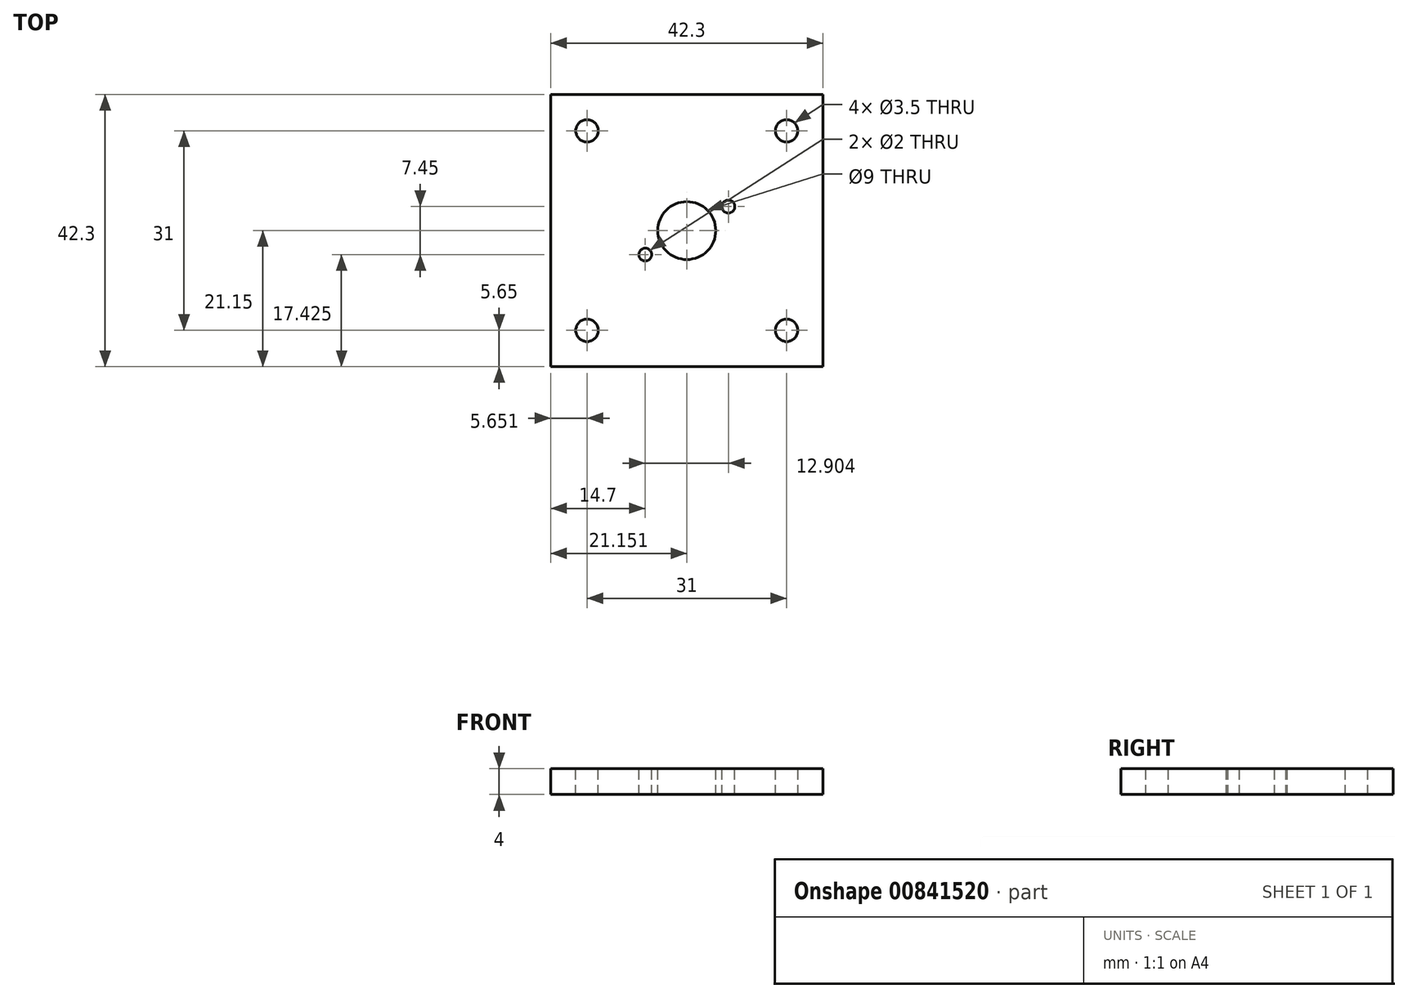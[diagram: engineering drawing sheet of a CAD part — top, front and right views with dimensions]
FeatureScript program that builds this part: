
annotation { "Feature Type Name" : "Feature", "Feature Type Description" : "" }
export const myFeature = defineFeature(function(context is Context, id is Id, definition is map)
    precondition{}
    {
        {
            var Q0;
            Q0=qCreatedBy(makeId("Top.planeOp"),FACE);
            var sketch = newSketch(context, id + "F0", { "sketchPlane" : qUnion([Q0])});
            skLineSegment(sketch, "E0.bottom", {"start": v(-22.2, 20.42) * mm, "end": v(20.1, 20.42) * mm});
            skLineSegment(sketch, "E0.top", {"start": v(-22.2, -21.88) * mm, "end": v(20.1, -21.88) * mm});
            skLineSegment(sketch, "E0.left", {"start": v(-22.2, 20.42) * mm, "end": v(-22.2, -21.88) * mm});
            skLineSegment(sketch, "E0.right", {"start": v(20.1, 20.42) * mm, "end": v(20.1, -21.88) * mm});
            skSolve(sketch);
        }
        {
            var Q0;
            Q0=makeQuery(id+"F0.imprint","IMPRINT",FACE,{"disambiguationData":[TD([[makeQuery(id+"F0.imprint","IMPRINT",EDGE,{"derivedFrom":sQuery(id+"F0.wireOp",EDGE,"E0.bottom")}),-1.0]])]});
            extrude(context, id + "F1", {"entities" : qUnion([Q0]), "depth" : 4 * mm, "offsetDistance" : 25 * mm});
        }
        {
            var Q0;
            Q0=makeQuery(id+"F1.opExtrude","CAP_FACE",FACE,{"disambiguationData":[OSD([sQuery(id+"F0.wireOp",EDGE,"E0.bottom"),sQuery(id+"F0.wireOp",EDGE,"E0.top"),sQuery(id+"F0.wireOp",EDGE,"E0.left"),sQuery(id+"F0.wireOp",EDGE,"E0.right")])],"isStart":false});
            var sketch = newSketch(context, id + "F2", { "sketchPlane" : qUnion([Q0])});
            skCircle(sketch, "E1", {"center": v(-16.55, -16.23) * mm, "radius": 1.75 * mm});
            skCircle(sketch, "E2", {"center": v(14.45, -16.23) * mm, "radius": 1.75 * mm});
            skCircle(sketch, "E3", {"center": v(14.45, 14.77) * mm, "radius": 1.75 * mm});
            skCircle(sketch, "E4", {"center": v(-16.55, 14.77) * mm, "radius": 1.75 * mm});
            skCircle(sketch, "E5", {"center": v(-1.05, -0.73) * mm, "radius": 4.5 * mm});
            skCircle(sketch, "E6", {"center": v(-7.5, -4.46) * mm, "radius": 1 * mm});
            skCircle(sketch, "E7", {"center": v(5.4, 3) * mm, "radius": 1 * mm});
            skSolve(sketch);
        }
        {
            var Q0;
            Q0=qSketchRegion(id+"F2",true);
            extrude(context, id + "F3", {"entities" : qUnion([Q0]), "operationType" : NewBodyOperationType.REMOVE, "oppositeDirection" : true, "depth" : 25 * mm, "offsetDistance" : 25 * mm});
        }
    });
